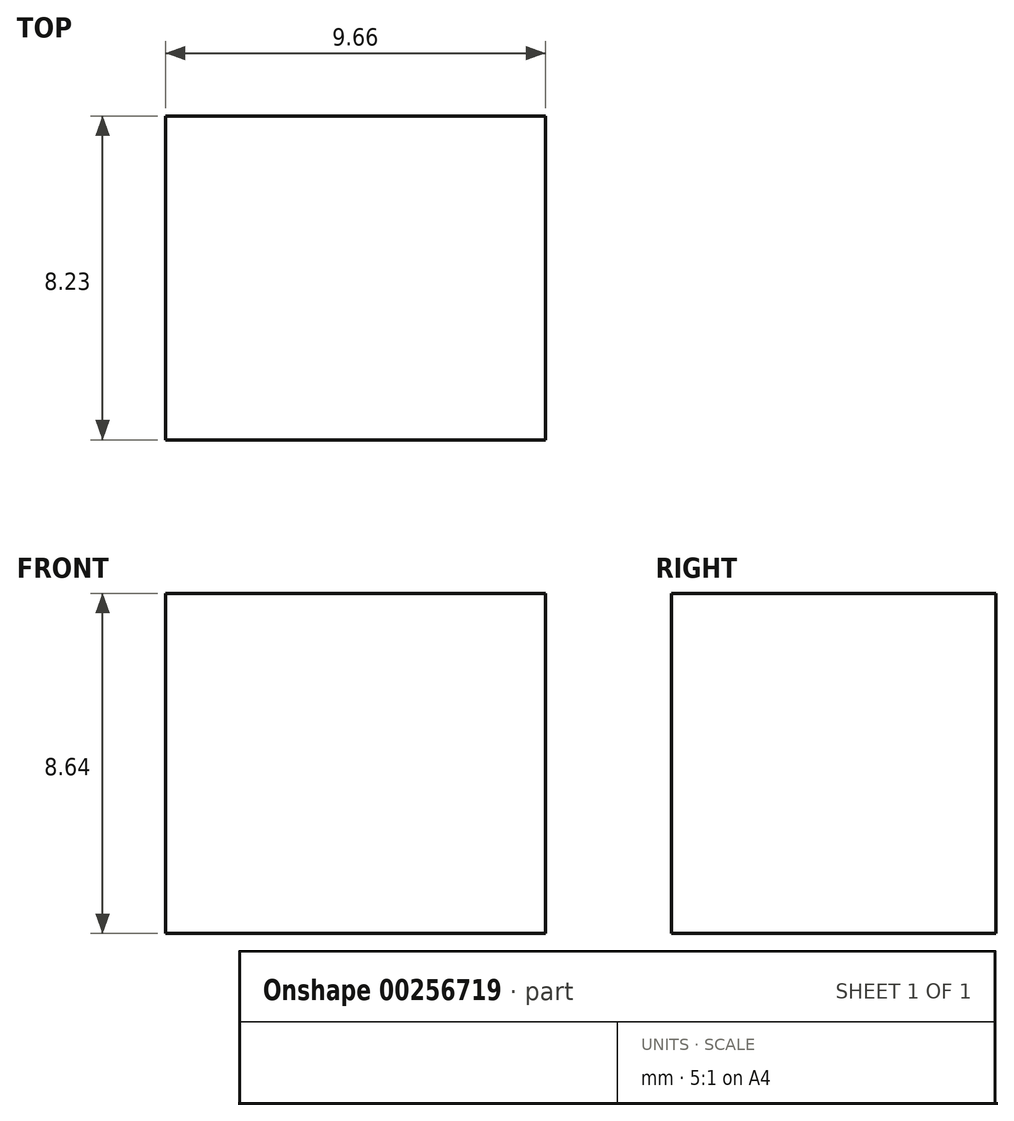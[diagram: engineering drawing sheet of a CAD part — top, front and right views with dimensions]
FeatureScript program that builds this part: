
annotation { "Feature Type Name" : "Feature", "Feature Type Description" : "" }
export const myFeature = defineFeature(function(context is Context, id is Id, definition is map)
    precondition{}
    {
        {
            var Q0;
            Q0=qCreatedBy(makeId("Top.planeOp"),FACE);
            var sketch = newSketch(context, id + "F0", { "sketchPlane" : qUnion([Q0])});
            skLineSegment(sketch, "E0.bottom", {"start": v(-9.66, -6.98) * mm, "end": v(0, -6.98) * mm});
            skLineSegment(sketch, "E0.top", {"start": v(-9.66, -15.21) * mm, "end": v(0, -15.21) * mm});
            skLineSegment(sketch, "E0.left", {"start": v(0, -15.21) * mm, "end": v(0, -6.98) * mm});
            skLineSegment(sketch, "E0.right", {"start": v(-9.66, -15.21) * mm, "end": v(-9.66, -6.98) * mm});
            skSolve(sketch);
        }
        {
            var Q0;
            Q0 = qSketchRegion(id + "F0", true);
            extrude(context, id + "F1", {"entities" : qUnion([Q0]), "depth" : 8.64 * mm});
        }
    });
